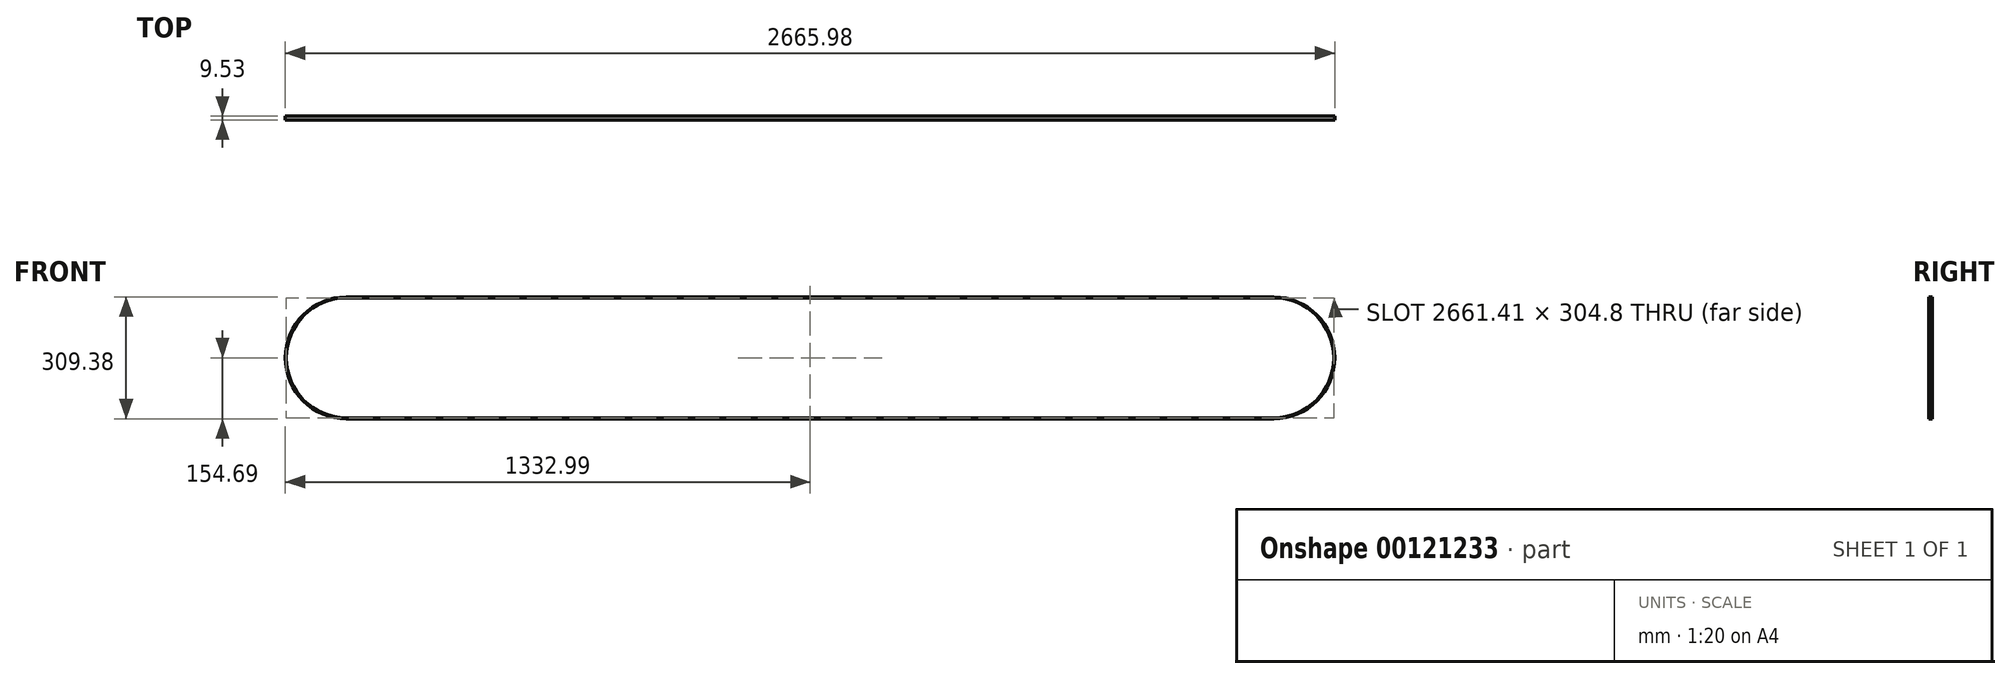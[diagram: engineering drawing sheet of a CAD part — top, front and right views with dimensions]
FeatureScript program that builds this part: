
annotation { "Feature Type Name" : "Feature", "Feature Type Description" : "" }
export const myFeature = defineFeature(function(context is Context, id is Id, definition is map)
    precondition{}
    {
        {
            var Q0;
            Q0=qCreatedBy(makeId("Front.planeOp"),FACE);
            var sketch = newSketch(context, id + "F0", { "sketchPlane" : qUnion([Q0])});
            skArc(sketch, "E0", {"start": v(-1050.93, 152.4) * mm, "mid": v(-1203.33, 0) * mm, "end": v(-1050.92, -152.4) * mm});
            skArc(sketch, "E1", {"start": v(1305.69, -152.4) * mm, "mid": v(1458.09, 0) * mm, "end": v(1305.69, 152.4) * mm});
            skLineSegment(sketch, "E2", {"start": v(-1050.93, 0) * mm, "end": v(-1050.93, -152.4) * mm, "construction": true});
            skLineSegment(sketch, "E3", {"start": v(-1050.93, -152.4) * mm, "end": v(-1050.93, 152.4) * mm, "construction": true});
            skLineSegment(sketch, "E4", {"start": v(1305.69, 0) * mm, "end": v(1305.69, -152.4) * mm, "construction": true});
            skLineSegment(sketch, "E5", {"start": v(1305.69, -152.4) * mm, "end": v(1305.69, 152.4) * mm, "construction": true});
            skLineSegment(sketch, "E6", {"start": v(-1050.92, -152.4) * mm, "end": v(1305.69, -152.4) * mm});
            skLineSegment(sketch, "E7", {"start": v(-1050.92, 152.4) * mm, "end": v(1305.69, 152.4) * mm});
            skArc(sketch, "E8.0", {"start": v(-1050.93, 154.69) * mm, "mid": v(-1205.61, 0) * mm, "end": v(-1050.93, -154.69) * mm});
            skLineSegment(sketch, "E8.1", {"start": v(-1050.92, 154.69) * mm, "end": v(1305.69, 154.69) * mm});
            skArc(sketch, "E8.2", {"start": v(1305.69, -154.69) * mm, "mid": v(1460.37, 0) * mm, "end": v(1305.69, 154.69) * mm});
            skLineSegment(sketch, "E8.3", {"start": v(-1050.92, -154.69) * mm, "end": v(1305.69, -154.69) * mm});
            skSolve(sketch);
        }
        {
            var Q0;
            Q0=makeQuery(id+"F0.imprint","IMPRINT",FACE,{"disambiguationData":[TD([[makeQuery(id+"F0.imprint","IMPRINT",EDGE,{"derivedFrom":sQuery(id+"F0.wireOp",EDGE,"E0")}),-1.0]])]});
            extrude(context, id + "F1", {"entities" : qUnion([Q0]), "depth" : 9.52 * mm});
        }
    });
